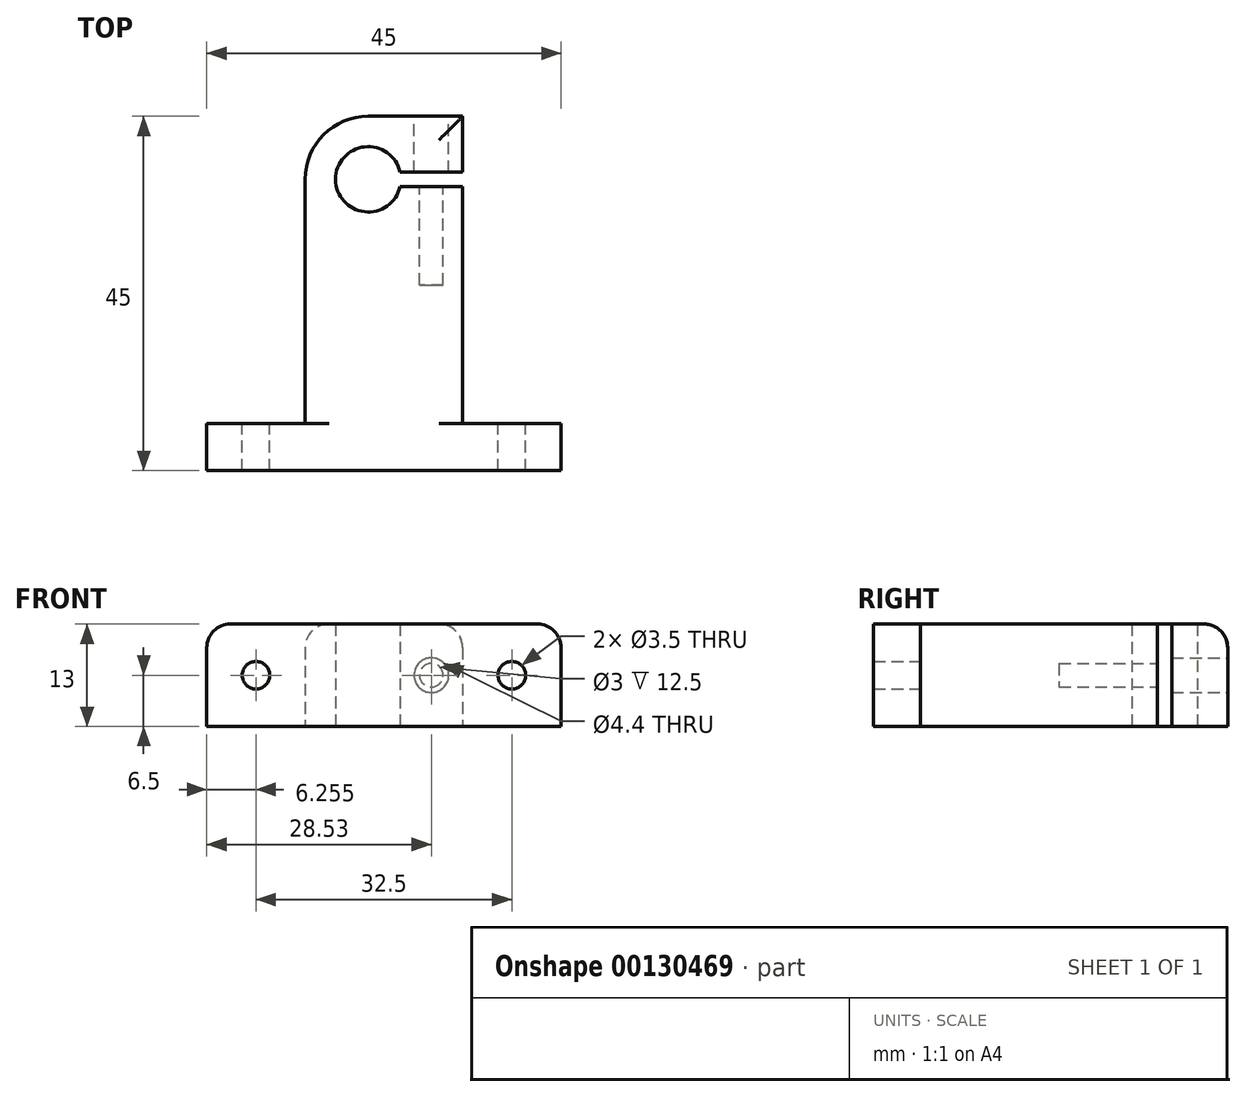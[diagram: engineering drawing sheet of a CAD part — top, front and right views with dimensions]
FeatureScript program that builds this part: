
annotation { "Feature Type Name" : "Feature", "Feature Type Description" : "" }
export const myFeature = defineFeature(function(context is Context, id is Id, definition is map)
    precondition{}
    {
        {
            var Q0;
            Q0=qCreatedBy(makeId("Top.planeOp"),FACE);
            var sketch = newSketch(context, id + "F0", { "sketchPlane" : qUnion([Q0])});
            skLineSegment(sketch, "E0", {"start": v(-31.59, -17.88) * mm, "end": v(13.41, -17.88) * mm});
            skLineSegment(sketch, "E1", {"start": v(13.41, -17.88) * mm, "end": v(13.41, -11.88) * mm});
            skLineSegment(sketch, "E2", {"start": v(13.41, -11.88) * mm, "end": v(0.91, -11.88) * mm});
            skLineSegment(sketch, "E3", {"start": v(0.91, -11.88) * mm, "end": v(0.91, 18.2) * mm});
            skLineSegment(sketch, "E4", {"start": v(0.91, 27.12) * mm, "end": v(-11.09, 27.12) * mm});
            skLineSegment(sketch, "E5", {"start": v(-19.09, 19.12) * mm, "end": v(-19.09, -11.88) * mm});
            skLineSegment(sketch, "E6", {"start": v(-19.09, -11.88) * mm, "end": v(-31.59, -11.88) * mm});
            skLineSegment(sketch, "E7", {"start": v(-31.59, -11.88) * mm, "end": v(-31.59, -17.88) * mm});
            skArc(sketch, "E8", {"start": v(-7.04, 20.03) * mm, "mid": v(-15.24, 19.12) * mm, "end": v(-7.04, 18.2) * mm});
            skPoint(sketch, "E9.visualSharp", {"position": v(-19.09, 27.12) * mm});
            skArc(sketch, "E9.filletArc", {"start": v(-11.09, 27.12) * mm, "mid": v(-16.74, 24.77) * mm, "end": v(-19.09, 19.12) * mm});
            skLineSegment(sketch, "E10.bottom", {"start": v(0.91, 18.2) * mm, "end": v(-7.04, 18.2) * mm});
            skLineSegment(sketch, "E10.top", {"start": v(0.91, 20.03) * mm, "end": v(-7.04, 20.03) * mm});
            skPoint(sketch, "E10.right.end.orphan", {"position": v(-23.8, 20.03) * mm});
            skPoint(sketch, "E10.right.start.orphan", {"position": v(-23.8, 18.2) * mm});
            skLineSegment(sketch, "E11.trimOffspring", {"start": v(0.91, 20.03) * mm, "end": v(0.91, 27.12) * mm});
            skSolve(sketch);
        }
        {
            var Q0;
            Q0 = qSketchRegion(id + "F0", true);
            extrude(context, id + "F1", {"entities" : qUnion([Q0]), "depth" : 13 * mm});
        }
        {
            var Q0;
            Q0=makeQuery(id+"F1.opExtrude","SWEPT_FACE",FACE,{"disambiguationData":[OSD([sQuery(id+"F0.wireOp",EDGE,"E10.bottom")])]});
            var sketch = newSketch(context, id + "F2", { "sketchPlane" : qUnion([Q0])});
            skCircle(sketch, "E12", {"center": v(3.06, 6.5) * mm, "radius": 1.5 * mm});
            skPoint(sketch, "E12.centerSnap0", {"position": v(-0.91, 6.5) * mm});
            skPoint(sketch, "E12.centerSnap1", {"position": v(3.06, 0) * mm});
            skSolve(sketch);
        }
        {
            var Q0;
            Q0 = qSketchRegion(id + "F2", true);
            extrude(context, id + "F3", {"entities" : qUnion([Q0]), "operationType" : NewBodyOperationType.REMOVE, "endBound" : BoundingType.SYMMETRIC, "oppositeDirection" : true, "depth" : 25 * mm});
        }
        {
            var Q0;
            Q0=makeQuery(id+"F1.opExtrude","SWEPT_FACE",FACE,{"disambiguationData":[OSD([sQuery(id+"F0.wireOp",EDGE,"E4")])]});
            var sketch = newSketch(context, id + "F4", { "sketchPlane" : qUnion([Q0])});
            skCircle(sketch, "E13", {"center": v(3.06, 6.5) * mm, "radius": 2.2 * mm});
            skSolve(sketch);
        }
        {
            var Q0;
            Q0 = qSketchRegion(id + "F4", true);
            extrude(context, id + "F5", {"entities" : qUnion([Q0]), "operationType" : NewBodyOperationType.REMOVE, "oppositeDirection" : true, "depth" : 8 * mm});
        }
        {
            var Q0;
            Q0=makeQuery(id+"F1.opExtrude","SWEPT_FACE",FACE,{"disambiguationData":[OSD([sQuery(id+"F0.wireOp",EDGE,"E2")])]});
            var sketch = newSketch(context, id + "F6", { "sketchPlane" : qUnion([Q0])});
            skCircle(sketch, "E14", {"center": v(-7.16, 6.5) * mm, "radius": 1.75 * mm});
            skPoint(sketch, "E14.centerSnap0", {"position": v(-7.16, 13) * mm});
            skPoint(sketch, "E14.centerSnap1", {"position": v(-13.41, 6.5) * mm});
            skSolve(sketch);
        }
        {
            var Q0;
            Q0=makeQuery(id+"F1.opExtrude","SWEPT_FACE",FACE,{"disambiguationData":[OSD([sQuery(id+"F0.wireOp",EDGE,"E6")])]});
            var sketch = newSketch(context, id + "F7", { "sketchPlane" : qUnion([Q0])});
            skCircle(sketch, "E15", {"center": v(25.34, 6.5) * mm, "radius": 1.75 * mm});
            skPoint(sketch, "E15.centerSnap0", {"position": v(31.59, 6.5) * mm});
            skPoint(sketch, "E15.centerSnap1", {"position": v(25.34, 13) * mm});
            skSolve(sketch);
        }
        {
            var Q0;
            Q0 = qSketchRegion(id + "F7", true);
            var Q1;
            Q1=makeQuery(id+"F6.imprint","IMPRINT",FACE,{"disambiguationData":[TD([[makeQuery(id+"F6.imprint","IMPRINT",EDGE,{"derivedFrom":sQuery(id+"F6.wireOp",EDGE,"E14")}),1.0]])]});
            extrude(context, id + "F8", {"entities" : qUnion([Q0, Q1]), "operationType" : NewBodyOperationType.REMOVE, "oppositeDirection" : true, "depth" : 25 * mm});
        }
        {
            var Q0;
            Q0=makeQuery(id+"F1.opExtrude","CAP_EDGE",EDGE,{"disambiguationData":[OSD([sQuery(id+"F0.wireOp",EDGE,"E1")])],"isStart":false});
            var Q1;
            Q1=makeQuery(id+"F1.opExtrude","CAP_EDGE",EDGE,{"disambiguationData":[OSD([sQuery(id+"F0.wireOp",EDGE,"E7")])],"isStart":false});
            var Q2;
            Q2=makeQuery(id+"F1.opExtrude","CAP_EDGE",EDGE,{"disambiguationData":[OSD([sQuery(id+"F0.wireOp",EDGE,"E3")])],"isStart":false});
            var Q3;
            Q3=makeQuery(id+"F1.opExtrude","CAP_EDGE",EDGE,{"disambiguationData":[OSD([sQuery(id+"F0.wireOp",EDGE,"E11.trimOffspring")])],"isStart":false});
            var Q4;
            Q4=makeQuery(id+"F1.opExtrude","CAP_EDGE",EDGE,{"disambiguationData":[OSD([sQuery(id+"F0.wireOp",EDGE,"E5")])],"isStart":false});
            fillet(context, id + "F9", {"entities" : qUnion([Q0, Q1, Q2, Q3, Q4]), "radius" : 3 * mm, "tangentPropagation" : true, "allowEdgeOverflow" : false});
        }
    });
